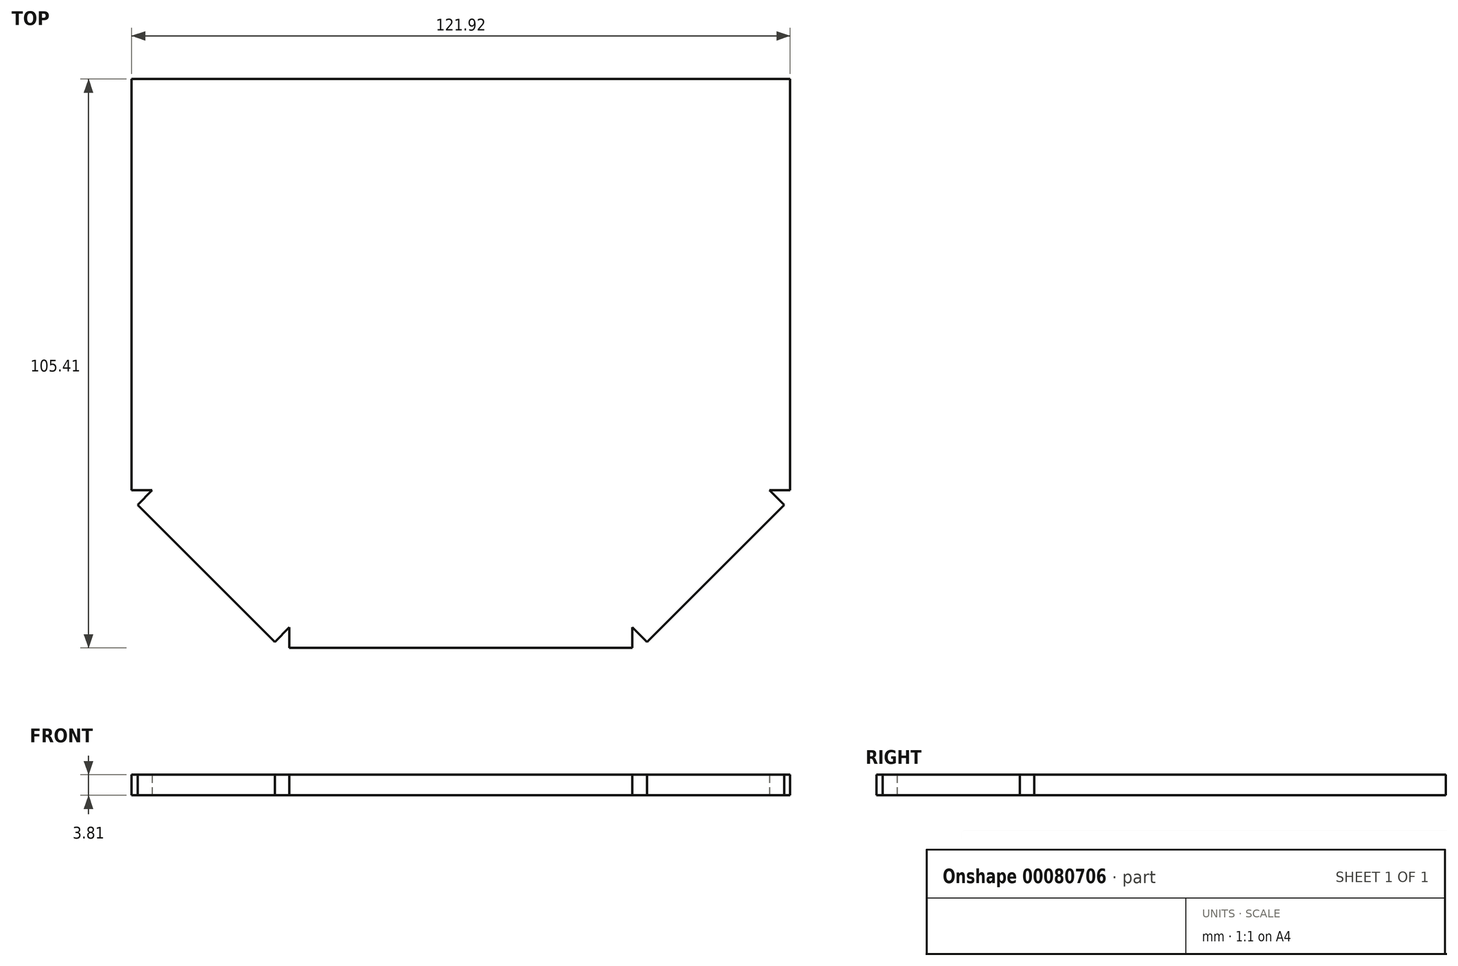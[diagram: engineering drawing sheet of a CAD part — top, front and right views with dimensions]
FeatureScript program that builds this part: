
annotation { "Feature Type Name" : "Feature", "Feature Type Description" : "" }
export const myFeature = defineFeature(function(context is Context, id is Id, definition is map)
    precondition{}
    {
        {
            var Q0;
            Q0=qCreatedBy(makeId("Top.planeOp"),FACE);
            var sketch = newSketch(context, id + "F0", { "sketchPlane" : qUnion([Q0])});
            skLineSegment(sketch, "E0.bottom", {"start": v(57.15, -38.1) * mm, "end": v(-57.15, -38.1) * mm, "construction": true});
            skLineSegment(sketch, "E0.top", {"start": v(57.15, 38.1) * mm, "end": v(-57.15, 38.1) * mm});
            skLineSegment(sketch, "E0.left", {"start": v(57.15, -38.1) * mm, "end": v(57.15, 38.1) * mm});
            skLineSegment(sketch, "E0.right", {"start": v(-57.15, -38.1) * mm, "end": v(-57.15, 38.1) * mm});
            skPoint(sketch, "E0.middle", {"position": v(0, 0) * mm});
            skLineSegment(sketch, "E1", {"start": v(0, -38.1) * mm, "end": v(0, -63.5) * mm, "construction": true});
            skPoint(sketch, "E1.endSnap0", {"position": v(0, -38.1) * mm});
            skLineSegment(sketch, "E2", {"start": v(0, -63.5) * mm, "end": v(-31.75, -63.5) * mm});
            skLineSegment(sketch, "E3", {"start": v(0, -63.5) * mm, "end": v(31.75, -63.5) * mm});
            skLineSegment(sketch, "E4", {"start": v(31.75, -63.5) * mm, "end": v(57.15, -38.1) * mm});
            skLineSegment(sketch, "E5", {"start": v(-31.75, -63.5) * mm, "end": v(-57.15, -38.1) * mm});
            skSolve(sketch);
        }
        {
            var Q0;
            Q0=makeQuery(id+"F0.imprint","IMPRINT",FACE,{"disambiguationData":[TD([[makeQuery(id+"F0.imprint","IMPRINT",EDGE,{"derivedFrom":sQuery(id+"F0.wireOp",EDGE,"E0.top")}),1.0]])]});
            extrude(context, id + "F1", {"entities" : qUnion([Q0]), "depth" : 3.8 * mm});
        }
        {
            var Q0;
            Q0=makeQuery(id+"F1.opExtrude","SWEPT_FACE",FACE,{"disambiguationData":[OSD([sQuery(id+"F0.wireOp",EDGE,"E2"),sQuery(id+"F0.wireOp",EDGE,"E3")])]});
            extrude(context, id + "F2", {"entities" : qUnion([Q0]), "operationType" : NewBodyOperationType.ADD, "depth" : 3.8 * mm});
        }
        {
            var Q0;
            Q0=makeQuery(id+"F1.opExtrude","SWEPT_FACE",FACE,{"disambiguationData":[OSD([sQuery(id+"F0.wireOp",EDGE,"E4")])]});
            extrude(context, id + "F3", {"entities" : qUnion([Q0]), "operationType" : NewBodyOperationType.ADD, "depth" : 3.8 * mm});
        }
        {
            var Q0;
            Q0=makeQuery(id+"F1.opExtrude","SWEPT_FACE",FACE,{"disambiguationData":[OSD([sQuery(id+"F0.wireOp",EDGE,"E5")])]});
            extrude(context, id + "F4", {"entities" : qUnion([Q0]), "operationType" : NewBodyOperationType.ADD, "depth" : 3.8 * mm});
        }
        {
            var Q0;
            Q0=makeQuery(id+"F1.opExtrude","SWEPT_FACE",FACE,{"disambiguationData":[OSD([sQuery(id+"F0.wireOp",EDGE,"E0.right")])]});
            extrude(context, id + "F5", {"entities" : qUnion([Q0]), "operationType" : NewBodyOperationType.ADD, "depth" : 3.8 * mm});
        }
        {
            var Q0;
            Q0=makeQuery(id+"F1.opExtrude","SWEPT_FACE",FACE,{"disambiguationData":[OSD([sQuery(id+"F0.wireOp",EDGE,"E0.left")])]});
            extrude(context, id + "F6", {"entities" : qUnion([Q0]), "operationType" : NewBodyOperationType.ADD, "depth" : 3.8 * mm});
        }
    });
